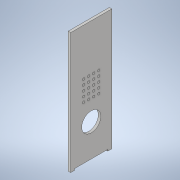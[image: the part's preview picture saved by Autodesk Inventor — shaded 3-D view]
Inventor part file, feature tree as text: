
AUTODESK INVENTOR PART (.ipt)
format: ipt  version: 2020 (Build 240168000, 168)  size: 141,312 bytes
history: native  units: mm
features: sketch x2, extrude x1
ambient origin geometry x8: Origin, YZ Plane, XZ Plane, XY Plane, X Axis, Y Axis, Z Axis, Center Point
bodies: Solid1 (feature_tree)
feature tree (3):
  sketch  "Sketch1"  dims[d0=241.0mm d1=82.0mm]
  sketch  "Sketch2"  dims[d2=38.0mm d3=41.0mm d4=174.0mm d5=66.0mm d6=3.0mm d7=8.0mm d21=4.7mm d22=50.0mm d24=10.0mm d25=40.0mm d27=10.0mm d32=5.0mm d33=0.0mm]
  extrude  "Extrusion1"  Depth=82.0mm
